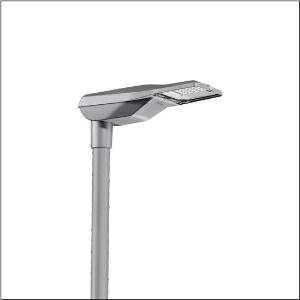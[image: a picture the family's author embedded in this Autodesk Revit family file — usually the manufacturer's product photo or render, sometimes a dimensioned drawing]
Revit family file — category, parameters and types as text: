
# Revit family: streetlight_sl_21_iq_micro___stw1_0a_5xe1e31d08cb_0f3c
name_source: partatom
category: Lighting Fixtures
units: mm (PartAtom-declared; Revit-internal decimal feet)

## family parameters
Cut with Voids When Loaded = No
Host = Face
Light Source = No
Part Type = Normal
Room Calculation Point = No
Round Connector Dimension = Use Diameter
Shared = No

## types (1)
- --- (1 x LED, 2870 lm, 19.4 W, 3000K)
    Apparent Load = 19 VA
    CIE Flux Codes = 38 75 98 100 100
    Color Rendering = 70
    Color Temperature = 3000K
    Default Elevation = 1800 mm
    Description = Streetlight SL 21 iQ micro, mast luminaire, primary light control with lens, of PMMA, primary optical cover: cover, of toughened safety glass, transparent, light distribution: STW1.0a, light emission: direct distribution, primary light characteristic: asymmetric, installation type: post-top, side-entry, LED, High Power LED, rated luminous flux: 2.870lm, luminous efficacy: 148lm/W, light colour: 730, colour temperature: 3000K, control: Auto-Match, Temp-Guard, Lumen-Switch, Night-Set, Smart-Wire, Light-Fading, Desk-Remote (wireless, voltage-free reading and setting of iQ features in the workshop via application-optimized NFC function/RFID function), optimised constant luminous flux control (CLO 2.0), presetting dimming linear, mains connection: 220..240V, AC, 50/60Hz, start of lifetime: 19W, end of service life: 20W, reduction: 10W, luminaire housing, of diecast aluminium, powder-coated, Siteco® metallic grey (DB 702S), corrosivity category C5 mid according to DIN EN ISO 12944, please order mast flange separately, inclination adjustable: 0°, 5°, 10°, 15°, sealing non-destructively replaceable, multi-level sealing system, length: 528mm, width: 235mm, height: 110mm, mast flange for spigot size: 42mm (side-entry): 5XC10008XM4, 60/48mm (side-entry/post-top): 5XC10108XM2, 76/60mm (side-entry/post-top): 5XC10108XM1, protection rating (complete): IP66, insulation class (complete): insulation class II (safety insulation), certification: CE, ENEC, ENEC+, VDE, impact resistance: IK09, permissible operating ambient temperature for outdoor applications: -40..+50°C, standard-compliant lighting for roads and squares, packaging unit: 1 piece

Light Distribution: STW1.0a
    Height = 110 mm
    Lamp = 1 x LED
    Lamp Light Flux = 2870 lm
    Lamp Power = 19.4 W
    Lamp count = 1
    Length = 528 mm
    Luminous efficacy = 148 lm/W
    Manufacturer = Siteco
    ModVariant = No
    Model = 5XE1E31D08CB
    Number of Poles = 1
    OnlyDefault = Yes
    Power Factor = 1
    Product Name = Streetlight SL 21 iQ micro | STW1.0a
    Product group = mast luminaire | pylon top
    ProductGroupID = 6100
    Protection Class = Protection class II
    Protection Degree = IP 66
    RLX_Detail_Level = 1
    RLX_Emergency_Light_Flux = 0 lm
    RLX_Emergency_Type = 0
    RLX_Emergency_Type_DB = No
    RlxData = <blob elided: 98597 chars, md5=2d5c13c8>
    Socket = socket
    Standby Power = 0 W
    System Light Flux = 2870 lm
    System Power = 19 W
    Type Comments = factory setting: luminous flux: 100 % | dim-lin: 254 | 387 mA
    Type Image = l_1006881.jpg
    URL = http://relux.com
    VarID = @adj_070221
    Voltage = 0 V
    Weight = 0.00 kg
    Width = 235 mm

## geometry (parser evidence)
native form markers: Blend x4, Sweep x9
no freeform markers — native parametric forms only
